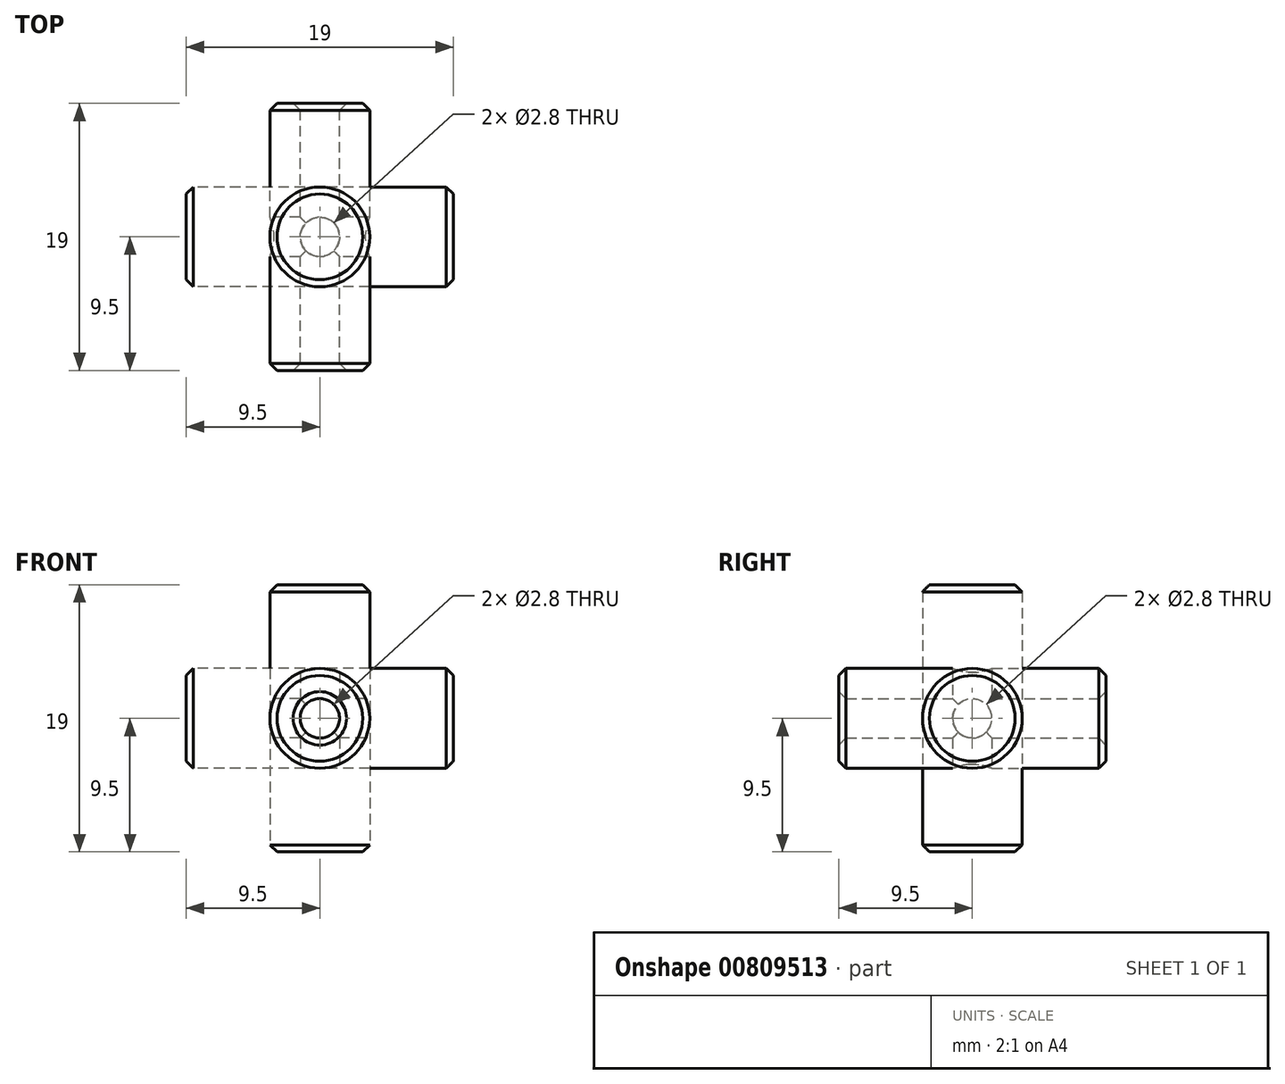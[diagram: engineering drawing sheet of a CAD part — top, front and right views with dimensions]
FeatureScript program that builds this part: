
annotation { "Feature Type Name" : "Feature", "Feature Type Description" : "" }
export const myFeature = defineFeature(function(context is Context, id is Id, definition is map)
    precondition{}
    {
        {
            var Q0;
            Q0=qCreatedBy(makeId("Front.planeOp"),FACE);
            var sketch = newSketch(context, id + "F0", { "sketchPlane" : qUnion([Q0])});
            skCircle(sketch, "E0", {"center": v(0, 0) * mm, "radius": 3.55 * mm});
            skSolve(sketch);
        }
        {
            var Q0;
            Q0=makeQuery(id+"F0.imprint","IMPRINT",FACE,{"disambiguationData":[TD([[makeQuery(id+"F0.imprint","IMPRINT",EDGE,{"derivedFrom":sQuery(id+"F0.wireOp",EDGE,"E0")}),1.0]])]});
            extrude(context, id + "F1", {"entities" : qUnion([Q0]), "endBound" : BoundingType.SYMMETRIC, "depth" : 19 * mm, "offsetDistance" : 25 * mm});
        }
        {
            var Q0;
            Q0=qCreatedBy(makeId("Front.planeOp"),FACE);
            var sketch = newSketch(context, id + "F2", { "sketchPlane" : qUnion([Q0])});
            skCircle(sketch, "E1", {"center": v(0, 0) * mm, "radius": 1.4 * mm});
            skSolve(sketch);
        }
        {
            var Q0;
            Q0 = qSketchRegion(id + "F2", true);
            extrude(context, id + "F3", {"entities" : qUnion([Q0]), "endBound" : BoundingType.SYMMETRIC, "depth" : 20 * mm, "offsetDistance" : 25 * mm});
        }
        {
            var Q0;
            Q0=qCreatedBy(makeId("Front.planeOp"),FACE);
            var sketch = newSketch(context, id + "F4", { "sketchPlane" : qUnion([Q0])});
            skLineSegment(sketch, "E2.bottom", {"start": v(0, 0) * mm, "end": v(10, 0) * mm});
            skLineSegment(sketch, "E2.top", {"start": v(0, 10) * mm, "end": v(10, 10) * mm});
            skLineSegment(sketch, "E2.left", {"start": v(0, 0) * mm, "end": v(0, 10) * mm});
            skLineSegment(sketch, "E2.right", {"start": v(10, 0) * mm, "end": v(10, 10) * mm});
            skSolve(sketch);
        }
        {
            var Q0;
            Q0=makeQuery(id+"F4.imprint","IMPRINT",FACE,{"disambiguationData":[TD([[makeQuery(id+"F4.imprint","IMPRINT",EDGE,{"derivedFrom":sQuery(id+"F4.wireOp",EDGE,"E2.bottom")}),1.0]])]});
            extrude(context, id + "F5", {"entities" : qUnion([Q0]), "depth" : 10 * mm, "offsetDistance" : 25 * mm});
        }
        {
            var Q0;
            Q0=qCreatedBy(makeId("Origin.pointOp"),VERTEX);
            var Q1;
            Q1=makeQuery(id+"F5.opExtrude","CAP_VERTEX",VERTEX,{"disambiguationData":[OSD([sQuery(id+"F4.wireOp",EDGE,"E2.top"),sQuery(id+"F4.wireOp",EDGE,"E2.right")])],"isStart":false});
            var Q2;
            Q2=makeQuery(id+"F5.opExtrude","CAP_VERTEX",VERTEX,{"disambiguationData":[OSD([sQuery(id+"F4.wireOp",EDGE,"E2.bottom"),sQuery(id+"F4.wireOp",EDGE,"E2.right")])],"isStart":false});
            cPlane(context, id + "F6", {"entities" : qUnion([Q0, Q1, Q2]), "cplaneType" : CPlaneType.THREE_POINT, "offset" : 25 * mm, "width" : 150 * mm, "height" : 150 * mm});
        }
        {
            var Q0;
            Q0=qCreatedBy(id+"F6.planeOp",FACE);
            var sketch = newSketch(context, id + "F7", { "sketchPlane" : qUnion([Q0])});
            skLineSegment(sketch, "E3", {"start": v(0, 0) * mm, "end": v(14.14, 10) * mm});
            skSolve(sketch);
        }
        {
            var Q0;
            Q0=makeQuery(id+"F5.opExtrude","SWEPT_BODY",BODY,{"disambiguationData":[OSD([sQuery(id+"F4.wireOp",EDGE,"E2.bottom"),sQuery(id+"F4.wireOp",EDGE,"E2.top"),sQuery(id+"F4.wireOp",EDGE,"E2.left"),sQuery(id+"F4.wireOp",EDGE,"E2.right")])]});
            deleteBodies(context, id + "F8", {"entities" : qUnion([Q0])});
        }
        {
            var Q0;
            Q0=makeQuery(id+"F3.opExtrude","SWEPT_BODY",BODY,{"disambiguationData":[OSD([sQuery(id+"F2.wireOp",EDGE,"E1")])]});
            var Q1;
            Q1=makeQuery(id+"F1.opExtrude","SWEPT_BODY",BODY,{"disambiguationData":[OSD([sQuery(id+"F0.wireOp",EDGE,"E0")])]});
            var Q2;
            Q2=sQuery(id+"F7.wireOp",EDGE,"E3");
            circularPattern(context, id + "F9", {"entities" : qUnion([Q0, Q1]), "axis" : qUnion([Q2]), "angle" : 360 * degree, "instanceCount" : 3, "equalSpace" : true});
        }
        {
            var Q0;
            Q0=makeQuery(id+"F3.opExtrude","SWEPT_BODY",BODY,{"disambiguationData":[OSD([sQuery(id+"F2.wireOp",EDGE,"E1")])]});
            var Q1;
            Q1=makeQuery(id+"F9.opPattern","COPY",BODY,{"derivedFrom":makeQuery(id+"F3.opExtrude","SWEPT_BODY",BODY,{"disambiguationData":[OSD([sQuery(id+"F2.wireOp",EDGE,"E1")])]}),"instanceName":"2"});
            var Q2;
            Q2=makeQuery(id+"F9.opPattern","COPY",BODY,{"derivedFrom":makeQuery(id+"F3.opExtrude","SWEPT_BODY",BODY,{"disambiguationData":[OSD([sQuery(id+"F2.wireOp",EDGE,"E1")])]}),"instanceName":"1"});
            var Q3;
            Q3=makeQuery(id+"F1.opExtrude","SWEPT_BODY",BODY,{"disambiguationData":[OSD([sQuery(id+"F0.wireOp",EDGE,"E0")])]});
            booleanBodies(context, id + "F10", {"operationType" : BooleanOperationType.SUBTRACTION, "tools" : qUnion([Q0, Q1, Q2]), "targets" : qUnion([Q3])});
        }
        {
            var Q0;
            Q0=makeQuery(id+"F9.opPattern","COPY",FACE,{"derivedFrom":makeQuery(id+"F1.opExtrude","CAP_FACE",FACE,{"disambiguationData":[OSD([sQuery(id+"F0.wireOp",EDGE,"E0")])],"isStart":false}),"instanceName":"2"});
            var Q1;
            Q1=makeQuery(id+"F1.opExtrude","CAP_FACE",FACE,{"disambiguationData":[OSD([sQuery(id+"F0.wireOp",EDGE,"E0")])],"isStart":false});
            var Q2;
            Q2=makeQuery(id+"F9.opPattern","COPY",FACE,{"derivedFrom":makeQuery(id+"F1.opExtrude","CAP_FACE",FACE,{"disambiguationData":[OSD([sQuery(id+"F0.wireOp",EDGE,"E0")])],"isStart":false}),"instanceName":"1"});
            var Q3;
            Q3=makeQuery(id+"F1.opExtrude","CAP_FACE",FACE,{"disambiguationData":[OSD([sQuery(id+"F0.wireOp",EDGE,"E0")])],"isStart":true});
            var Q4;
            Q4=makeQuery(id+"F9.opPattern","COPY",FACE,{"derivedFrom":makeQuery(id+"F1.opExtrude","CAP_FACE",FACE,{"disambiguationData":[OSD([sQuery(id+"F0.wireOp",EDGE,"E0")])],"isStart":true}),"instanceName":"2"});
            var Q5;
            Q5=makeQuery(id+"F9.opPattern","COPY",FACE,{"derivedFrom":makeQuery(id+"F1.opExtrude","CAP_FACE",FACE,{"disambiguationData":[OSD([sQuery(id+"F0.wireOp",EDGE,"E0")])],"isStart":true}),"instanceName":"1"});
            chamfer(context, id + "F11", {"entities" : qUnion([Q0, Q1, Q2, Q3, Q4, Q5]), "width" : 0.5 * mm, "tangentPropagation" : true});
        }
    });
